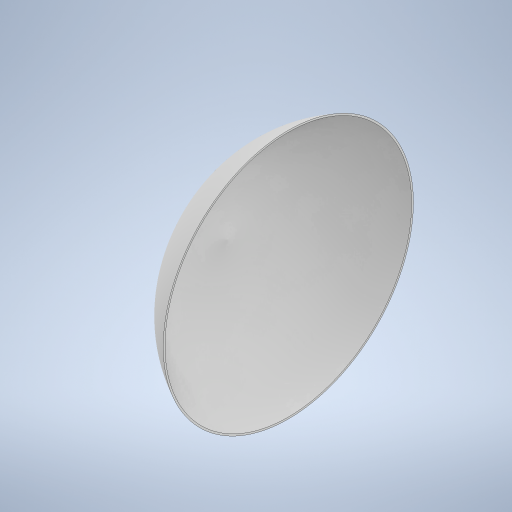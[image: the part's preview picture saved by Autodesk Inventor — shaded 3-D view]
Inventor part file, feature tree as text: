
AUTODESK INVENTOR PART (.ipt)
format: ipt  version: 2023 (Build 270158000, 158)  size: 629,248 bytes
history: native  units: mm
features: revolve x1, shell x1, sketch x1
ambient origin geometry x8: Origin, YZ Plane, XZ Plane, XY Plane, X Axis, Y Axis, Z Axis, Center Point
bodies: Solid1 (feature_tree)
feature tree (3):
  revolve  "Revolution1"  [1 undecoded]
  shell  "Shell1"  Thickness=90.0deg
  sketch  "Sketch1"  dims[d0=40.0mm d1=80.0mm d3=90.0deg d4=1.0mm d6=73.257611mm]
note: 1 required parameter value undecoded (feature->parameter linkage not recoverable at this tier; creation-order binding heuristic only, values carry confidence <= 0.55)
